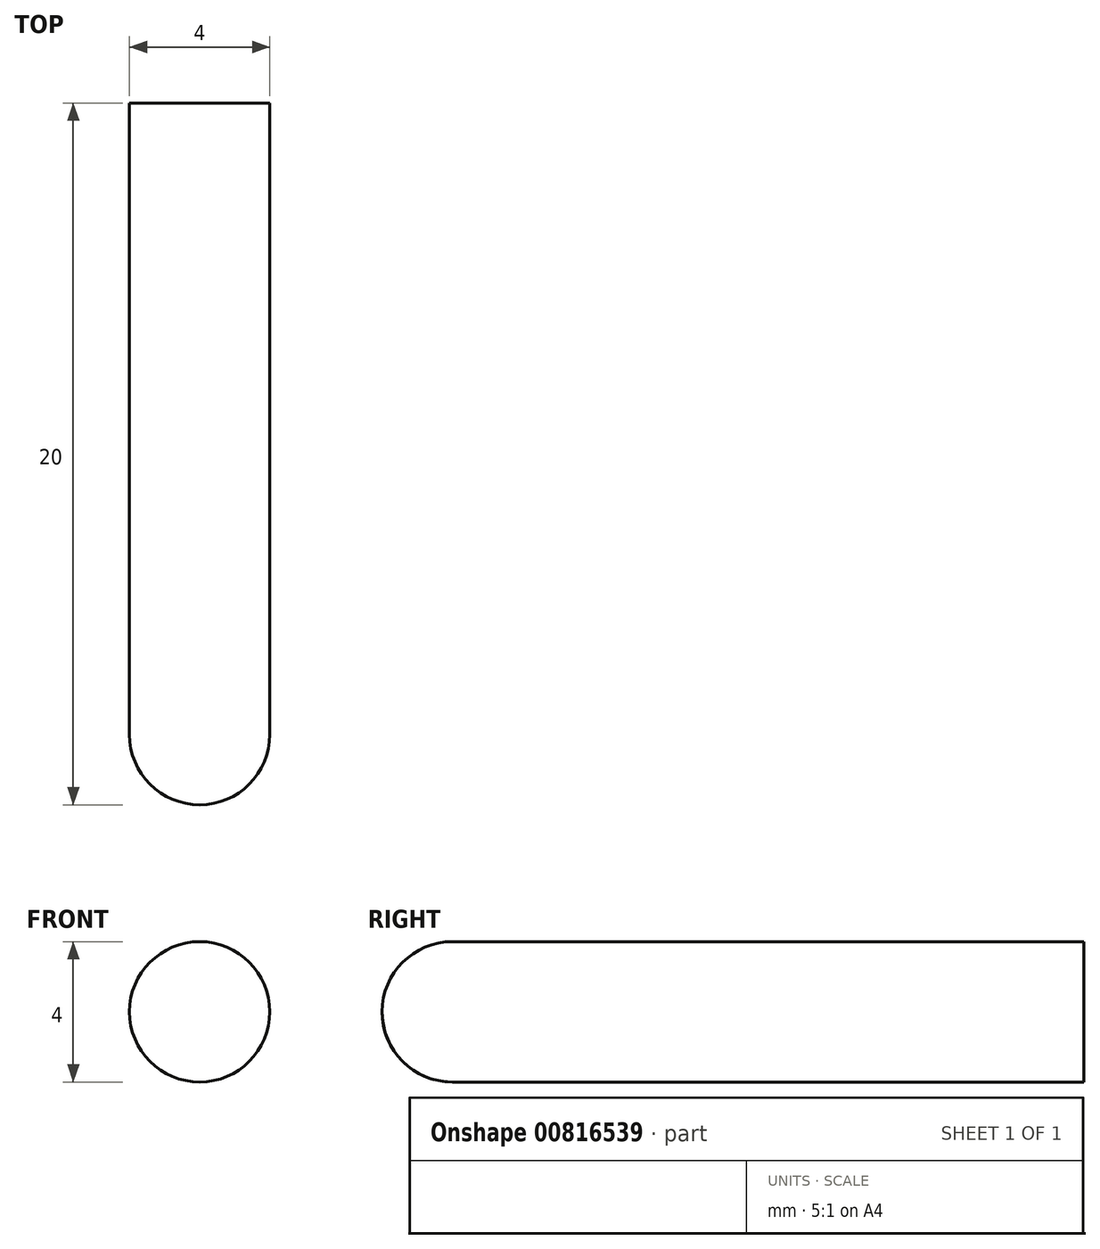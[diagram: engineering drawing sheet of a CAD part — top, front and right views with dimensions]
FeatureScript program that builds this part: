
annotation { "Feature Type Name" : "Feature", "Feature Type Description" : "" }
export const myFeature = defineFeature(function(context is Context, id is Id, definition is map)
    precondition{}
    {
        {
            assignVariable(context, id + "F0", {"name" : "Bolzenlaenge", "anyValue" : 20});
        }
        {
            var Q0;
            Q0=qCreatedBy(makeId("Front.planeOp"),FACE);
            var sketch = newSketch(context, id + "F1", { "sketchPlane" : qUnion([Q0])});
            skCircle(sketch, "E0", {"center": v(0, 0) * mm, "radius": 2 * mm});
            skSolve(sketch);
        }
        {
            var Q0;
            Q0=makeQuery(id+"F1.imprint","IMPRINT",FACE,{"disambiguationData":[TD([[makeQuery(id+"F1.imprint","IMPRINT",EDGE,{"derivedFrom":sQuery(id+"F1.wireOp",EDGE,"E0")}),1.0]])]});
            extrude(context, id + "F2", {"entities" : qUnion([Q0]), "depth" : (getVariable(context, 'Bolzenlaenge')) * mm, "offsetDistance" : 25 * mm});
        }
        {
            var Q0;
            Q0=makeQuery(id+"F2.opExtrude","CAP_FACE",FACE,{"disambiguationData":[OSD([sQuery(id+"F1.wireOp",EDGE,"E0")])],"isStart":false});
            fillet(context, id + "F3", {"entities" : qUnion([Q0]), "radius" : 2 * mm, "tangentPropagation" : true, "allowEdgeOverflow" : false});
        }
    });
